# Revit family: Metal_Lockers-Salsbury_Industries-61000_Series-1_Wide_Units
name_source: partatom
category: Specialty Equipment
units: mm (PartAtom-declared; Revit-internal decimal feet)

## family parameters
Always vertical = Yes
Classification Number = 23.40.00.00
Cut with Voids When Loaded = No
Enable Cutting in Views = No
Maintain Annotation Orientation = No
Part Type = Normal
Room Calculation Point = No
Round Connector Dimension = Use Diameter
Shared = No
Work Plane-Based = No

## types (18) — shared parameters
Assembly Code = C1030310
Building Codes = https://www.lockers.com
Construction Details = https://www.lockers.com
Green Building-LEED = https://www.arcat.com
Hasp Handle Material = Plastic - Salsbury Finish - Black
Hasp Plate Rivet Material = Steel -Salsbury Finish - Polished Steel
Installation-Fabrication = https://www.lockers.com
Keynote = 10 51 00
Manufacturer = Salsbury Industries
Manufacturer Fax = 1-800-562-5399
Manufacturer Website = https://www.lockers.com
MasterFormat Number = 10 51 13
MasterFormat Title = Lockers
OmniClass 23 Number = 23.40.00.00
OmniClass 23 Title = Equipment and Furnishings
Product Data = https://www.lockers.com
Revision = R1_2018-10
Sales Information = https://www.lockers.com
Specification = https://www.lockers.com
Test Data = https://www.lockers.com
Type Comments = Standard Metal Locker - Single Tier
URL = www.lockers.com
Version = 2.0 (06/30/17)
Width = 12.04 "
zero-valued in all types: Default Elevation

## per-type parameters (varying)
| type | Base Height | Depth | Description | Door Location D1 | Model | Sloping Hood Height | Standard Leg Base | Unit Height | Zee Base |
| 61162 - with Standard 6" High Legs | 6 " | 12.01 " | 1 Wide - 6 Feet High - 12 Inches Deep | Metal Locker Doors-12 inch with Hasps : Single Tier Door - 6 foot | 61162 | 6.625 " | Metal Locker Legs : 6" High - 12" W x 12" D | 72 " | Metal Locker Zee Base : None |
| 61165 - with Standard 6" High Legs | 6 " | 15.01 " | 1 Wide - 6 Feet High - 15 Inches Deep | Metal Locker Doors-12 inch with Hasps : Single Tier Door - 6 foot | 61165 | 8.682 " | Metal Locker Legs : 6" High - 12" W x 15" D | 72 " | Metal Locker Zee Base : None |
| 61168 - with Standard 6" High Legs | 6 " | 18.01 " | 1 Wide - 6 Feet High - 18 Inches Deep | Metal Locker Doors-12 inch with Hasps : Single Tier Door - 6 foot | 61168 | 10.739 " | Metal Locker Legs : 6" High - 12"W x 18"D | 72 " | Metal Locker Zee Base : None |
| 61162 - with 77572 Zee Base and 77550 Lockers without Legs | 4 " | 12.01 " | 1 Wide - 6 Feet High - 12 Inches Deep with Zee Base and Lockers without Legs | Metal Locker Doors-12 inch with Hasps : Single Tier Door - 6 foot | 61162 with 77572 and 77550 | 6.625 " | Metal Locker Legs : No Legs | 72 " | Metal Locker Zee Base : 77572- 12" W x 12" D |
| 61165 - with 77575 Zee Base and 77550 Lockers without Legs | 4 " | 15.01 " | 1 Wide - 6 Feet High - 15 Inches Deep with Zee Base and Lockers without Legs | Metal Locker Doors-12 inch with Hasps : Single Tier Door - 6 foot | 61165 with 77575 and 77550 | 8.682 " | Metal Locker Legs : No Legs | 72 " | Metal Locker Zee Base : 77575 - 12" W x 15" D |
| 61168 - with 77578 Zee Base and 77550 Lockers without Legs | 4 " | 18.01 " | 1 Wide - 6 Feet High - 18 Inches Deep with Zee Base and Lockers without Legs | Metal Locker Doors-12 inch with Hasps : Single Tier Door - 6 foot | 61168 with 77578 and 77550 | 10.739 " | Metal Locker Legs : No Legs | 72 " | Metal Locker Zee Base : 77578 - 12"W x 18"D |
| 61162 - with 77550 Lockers without Legs | 0 " | 12.01 " | 1 Wide - 6 Feet High - 12 Inches Deep with Lockers without Legs | Metal Locker Doors-12 inch with Hasps : Single Tier Door - 6 foot | 61162 with 77550 | 6.625 " | Metal Locker Legs : No Legs | 72 " | Metal Locker Zee Base : None |
| 61165 - with 77550 Lockers without Legs | 0 " | 15.01 " | 1 Wide - 6 Feet High - 15 Inches Deep with Lockers without Legs | Metal Locker Doors-12 inch with Hasps : Single Tier Door - 6 foot | 61165 with 77550 | 8.682 " | Metal Locker Legs : No Legs | 72 " | Metal Locker Zee Base : None |
| 61168 - with 77550 Lockers without Legs | 0 " | 18.01 " | 1 Wide - 6 Feet High - 18 Inches Deep with Lockers without Legs | Metal Locker Doors-12 inch with Hasps : Single Tier Door - 6 foot | 61168 with 77550 | 10.739 " | Metal Locker Legs : No Legs | 72 " | Metal Locker Zee Base : None |
| 61152 - with Standard 6" High Legs | 6 " | 12.01 " | 1 Wide - 5 Feet High - 12 Inches Deep | Metal Locker Doors-12 inch with Hasps : Single Tier Door - 5 foot | 61152 | 6.625 " | Metal Locker Legs : 6" High - 12" W x 12" D | 60 " | Metal Locker Zee Base : None |
| 61152 - with 77572 Zee Base and 77550 Lockers without Legs | 4 " | 12.01 " | 1 Wide - 5 Feet High - 12 Inches Deep with Zee Base and Lockers without Legs | Metal Locker Doors-12 inch with Hasps : Single Tier Door - 5 foot | 61152 with 77572 and 77550 | 6.625 " | Metal Locker Legs : No Legs | 60 " | Metal Locker Zee Base : 77572- 12" W x 12" D |
| 61152 - with 77550 Lockers without Legs | 0 " | 12.01 " | 1 Wide - 5 Feet High - 12 Inches Deep with Lockers without Legs | Metal Locker Doors-12 inch with Hasps : Single Tier Door - 5 foot | 61152 with 77550 | 6.625 " | Metal Locker Legs : No Legs | 60 " | Metal Locker Zee Base : None |
| 61155 - with Standard 6" High Legs | 6 " | 15.01 " | 1 Wide - 5 Feet High - 15 Inches Deep | Metal Locker Doors-12 inch with Hasps : Single Tier Door - 5 foot | 61155 | 8.682 " | Metal Locker Legs : 6" High - 12" W x 15" D | 60 " | Metal Locker Zee Base : None |
| 61155 - with 77575 Zee Base and 77550 Lockers without Legs | 4 " | 15.01 " | 1 Wide - 5 Feet High - 15 Inches Deep with Zee Base and Lockers without Legs | Metal Locker Doors-12 inch with Hasps : Single Tier Door - 5 foot | 61155 with 77575 and 77550 | 8.682 " | Metal Locker Legs : No Legs | 60 " | Metal Locker Zee Base : 77575 - 12" W x 15" D |
| 61155 - with 77550 Lockers without Legs | 0 " | 15.01 " | 1 Wide - 5 Feet High - 15 Inches Deep with Lockers without Legs | Metal Locker Doors-12 inch with Hasps : Single Tier Door - 5 foot | 61165 with 77550 | 8.682 " | Metal Locker Legs : No Legs | 60 " | Metal Locker Zee Base : None |
| 61158 - with Standard 6" High Legs | 6 " | 18.01 " | 1 Wide - 5 Feet High - 18 Inches Deep | Metal Locker Doors-12 inch with Hasps : Single Tier Door - 5 foot | 61158 | 10.739 " | Metal Locker Legs : 6" High - 12"W x 18"D | 60 " | Metal Locker Zee Base : None |
| 61158 - with 77578 Zee Base and 77550 Lockers without Legs | 4 " | 18.01 " | 1 Wide - 5 Feet High - 18 Inches Deep with Zee Base and Lockers without Legs | Metal Locker Doors-12 inch with Hasps : Single Tier Door - 5 foot | 61158 with 77578 and 77550 | 10.739 " | Metal Locker Legs : No Legs | 60 " | Metal Locker Zee Base : 77578 - 12"W x 18"D |
| 61158 - with 77550 Lockers without Legs | 0 " | 18.01 " | 1 Wide - 5 Feet High - 18 Inches Deep with Lockers without Legs | Metal Locker Doors-12 inch with Hasps : Single Tier Door - 5 foot | 61158 with 77550 | 10.739 " | Metal Locker Legs : No Legs | 60 " | Metal Locker Zee Base : None |

## geometry (parser evidence)
native form markers: Sweep x37
no freeform markers — native parametric forms only
